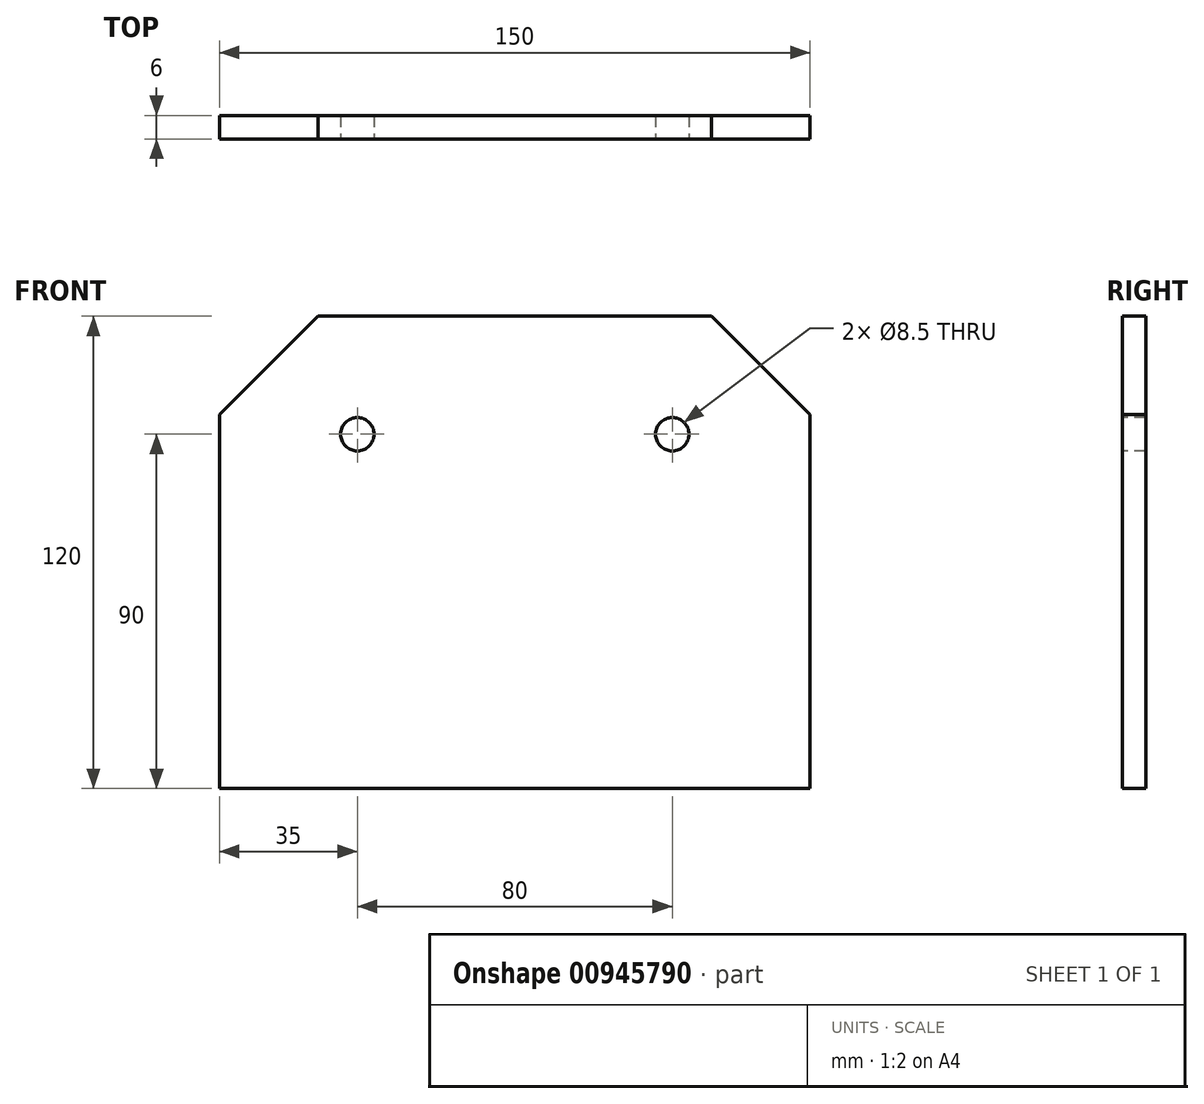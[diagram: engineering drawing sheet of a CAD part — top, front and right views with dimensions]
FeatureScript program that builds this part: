
annotation { "Feature Type Name" : "Feature", "Feature Type Description" : "" }
export const myFeature = defineFeature(function(context is Context, id is Id, definition is map)
    precondition{}
    {
        {
            var Q0;
            Q0=qCreatedBy(makeId("Front.planeOp"),FACE);
            var sketch = newSketch(context, id + "F0", { "sketchPlane" : qUnion([Q0])});
            skLineSegment(sketch, "E0.bottom", {"start": v(75, 60) * mm, "end": v(-75, 60) * mm});
            skLineSegment(sketch, "E0.top", {"start": v(75, -60) * mm, "end": v(-75, -60) * mm});
            skLineSegment(sketch, "E0.left", {"start": v(75, 60) * mm, "end": v(75, -60) * mm});
            skLineSegment(sketch, "E0.right", {"start": v(-75, 60) * mm, "end": v(-75, -60) * mm});
            skPoint(sketch, "E0.middle", {"position": v(0, 0) * mm});
            skSolve(sketch);
        }
        {
            var Q0;
            Q0 = qSketchRegion(id + "F0", true);
            extrude(context, id + "F1", {"entities" : qUnion([Q0]), "depth" : 6 * mm, "offsetDistance" : 25 * mm});
        }
        {
            var Q0;
            Q0=makeQuery(id+"F1.opExtrude","CAP_FACE",FACE,{"disambiguationData":[OSD([sQuery(id+"F0.wireOp",EDGE,"E0.bottom"),sQuery(id+"F0.wireOp",EDGE,"E0.top"),sQuery(id+"F0.wireOp",EDGE,"E0.left"),sQuery(id+"F0.wireOp",EDGE,"E0.right")])],"isStart":false});
            var sketch = newSketch(context, id + "F2", { "sketchPlane" : qUnion([Q0])});
            skCircle(sketch, "E1", {"center": v(-40, 30) * mm, "radius": 4.25 * mm});
            skLineSegment(sketch, "E2", {"start": v(0, 60) * mm, "end": v(0, -60) * mm});
            skCircle(sketch, "E3.MirrorC", {"center": v(40, 30) * mm, "radius": 4.25 * mm});
            skSolve(sketch);
        }
        {
            var Q0;
            Q0 = qSketchRegion(id + "F2", true);
            extrude(context, id + "F3", {"entities" : qUnion([Q0]), "operationType" : NewBodyOperationType.REMOVE, "oppositeDirection" : true, "depth" : 25 * mm, "offsetDistance" : 25 * mm});
        }
        {
            var Q0;
            Q0=makeQuery(id+"F1.opExtrude","SWEPT_EDGE",EDGE,{"disambiguationData":[OSD([sQuery(id+"F0.wireOp",EDGE,"E0.bottom"),sQuery(id+"F0.wireOp",EDGE,"E0.right")])]});
            var Q1;
            Q1=makeQuery(id+"F1.opExtrude","SWEPT_EDGE",EDGE,{"disambiguationData":[OSD([sQuery(id+"F0.wireOp",EDGE,"E0.bottom"),sQuery(id+"F0.wireOp",EDGE,"E0.left")])]});
            chamfer(context, id + "F4", {"entities" : qUnion([Q0, Q1]), "width" : 25 * mm, "tangentPropagation" : true});
        }
    });
